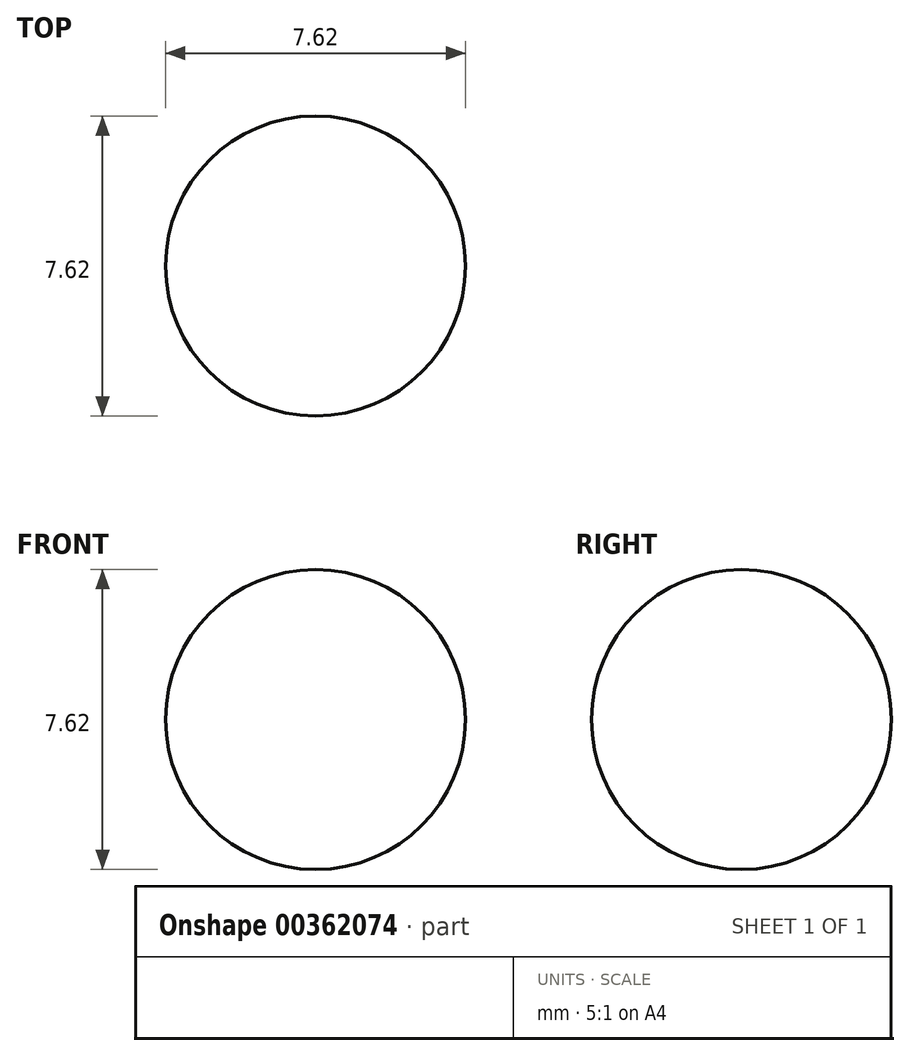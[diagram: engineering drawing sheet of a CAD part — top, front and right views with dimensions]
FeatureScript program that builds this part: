
annotation { "Feature Type Name" : "Feature", "Feature Type Description" : "" }
export const myFeature = defineFeature(function(context is Context, id is Id, definition is map)
    precondition{}
    {
        {
            var Q0;
            Q0=qCreatedBy(makeId("Front.planeOp"),FACE);
            var sketch = newSketch(context, id + "F0", { "sketchPlane" : qUnion([Q0])});
            skArc(sketch, "E0", {"start": v(0, 3.81) * mm, "mid": v(-3.81, 0) * mm, "end": v(0, -3.81) * mm});
            skPoint(sketch, "E1", {"position": v(0, 3.81) * mm});
            skPoint(sketch, "E2", {"position": v(0, -3.81) * mm});
            skLineSegment(sketch, "E3", {"start": v(0, 3.81) * mm, "end": v(0, -3.81) * mm});
            skSolve(sketch);
        }
        {
            var Q0;
            Q0=makeQuery(id+"F0.imprint","IMPRINT",FACE,{"disambiguationData":[TD([[makeQuery(id+"F0.imprint","IMPRINT",EDGE,{"derivedFrom":sQuery(id+"F0.wireOp",EDGE,"E0")}),1.0]])]});
            var Q1;
            Q1=sQuery(id+"F0.wireOp",EDGE,"E3");
            revolve(context, id + "F1", {"entities" : qUnion([Q0]), "axis" : qUnion([Q1]), "revolveType" : RevolveType.FULL});
        }
    });
